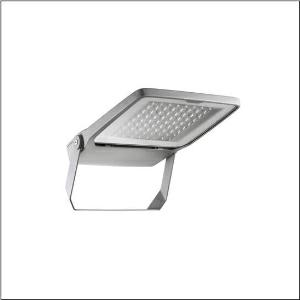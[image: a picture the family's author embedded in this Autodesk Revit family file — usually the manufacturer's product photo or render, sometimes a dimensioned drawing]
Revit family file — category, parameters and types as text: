
# Revit family: floodlight_fl_20_mini___pl52_5xa7672c1d1ac_04f0
name_source: partatom
category: Lighting Fixtures
units: mm (PartAtom-declared; Revit-internal decimal feet)

## family parameters
Cut with Voids When Loaded = No
Host = Face
Light Source = No
Part Type = Normal
Room Calculation Point = No
Round Connector Dimension = Use Diameter
Shared = No

## types (1)
- --- (1 x LED 3000K / CRI = 80 (unbekannt), 9640 lm, 3000K)
    Apparent Load = 96 VA
    CIE Flux Codes = 27 59 98 100 100
    Color Rendering = 80
    Color Temperature = 3000K
    Default Elevation = 1800 mm
    Description = Floodlight FL 20 mini, floodlight, primary light control with lens, of plastic, primary optical cover: protective disc, of toughened safety glass, transparent, light distribution: PL52, light emission: direct distribution, primary light characteristic: asymmetric, installation type: surface-mounted, LED, High Power LED, rated luminous flux: 9.640lm, luminous efficacy: 101lm/W, light colour: 830, colour temperature: 3000K, control gear: ECG Plus, control: flexible luminous flux parameterisation, time-dependent luminous flux control, digital communication interface, power reduction, overheat protection, electronic power reduction, with terminal, 5-pole, max. 2.5mm², mains connection: 220..240V, AC, 50/60Hz, rated input power: 96W, LED unit, of diecast aluminium, powder-coated, Siteco® metallic grey (DB 702S), corrosivity category C5 mid according to DIN EN ISO 12944, incl. 1x M20 cable gland for cable Ø 6.5..12mm, length: 446mm, width: 355mm, height: 62mm, housing frame, of diecast aluminium, powder-coated, Siteco® metallic grey (DB 702S), mounting bracket, of steel, powder-coated, Siteco® metallic grey (DB 702S), DALI, protection rating (complete): IP66, insulation class (complete): insulation class II (safety insulation), certification: CE, ENEC, VDE, protection symbol: D, permissible operating ambient temperature: -40..+40°C, permissible operating ambient temperature for outdoor applications: -40..+50°C, standard: DIN EN 12944, packaging unit: 1 piece

Light Distribution: PL52
    Height = 62 mm  [stored 0.203412 ft]
    Lamp = 1 x LED 3000K / CRI >= 80 (unbekannt)
    Lamp Light Flux = 9640 lm
    Lamp count = 1
    Length = 467 mm
    Luminous efficacy = 101 lm/W
    Manufacturer = Siteco
    ModVariant = No
    Model = 5XA7672C1D1AC
    Mounting Place = Wall
    Mounting Type = Surface mounted
    Number of Poles = 1
    OnlyDefault = Yes
    Power Factor = 1
    Product Name = Floodlight FL 20 mini | PL52
    Product group = floodlight | wall mounted
    ProductGroupID = 2001
    Protection Class = Protection class II
    Protection Degree = IP 66
    RLX_Detail_Level = 1
    RLX_Emergency_Light_Flux = 0 lm
    RLX_Emergency_Type = 0
    RLX_Emergency_Type_DB = No
    RlxData = <blob elided: 74233 chars, md5=d3dae6d2>
    Socket = socket
    Standby Power = 0 W
    System Light Flux = 9640 lm
    System Power = 96 W
    Type Comments = factory setting: luminous flux: 100 % | dim-lin: 254 | 500 mA
    Type Image = l_1005948.jpg
    URL = http://relux.com
    VarID = @adj_163921
    Voltage = 0 V
    Weight = 0.00 kg
    Width = 335 mm

note: [stored X ft] marks values corroborated as IEEE doubles in the binary element streams (Revit-internal decimal feet)

## geometry (parser evidence)
native form markers: Blend x4, Sweep x13
no freeform markers — native parametric forms only
